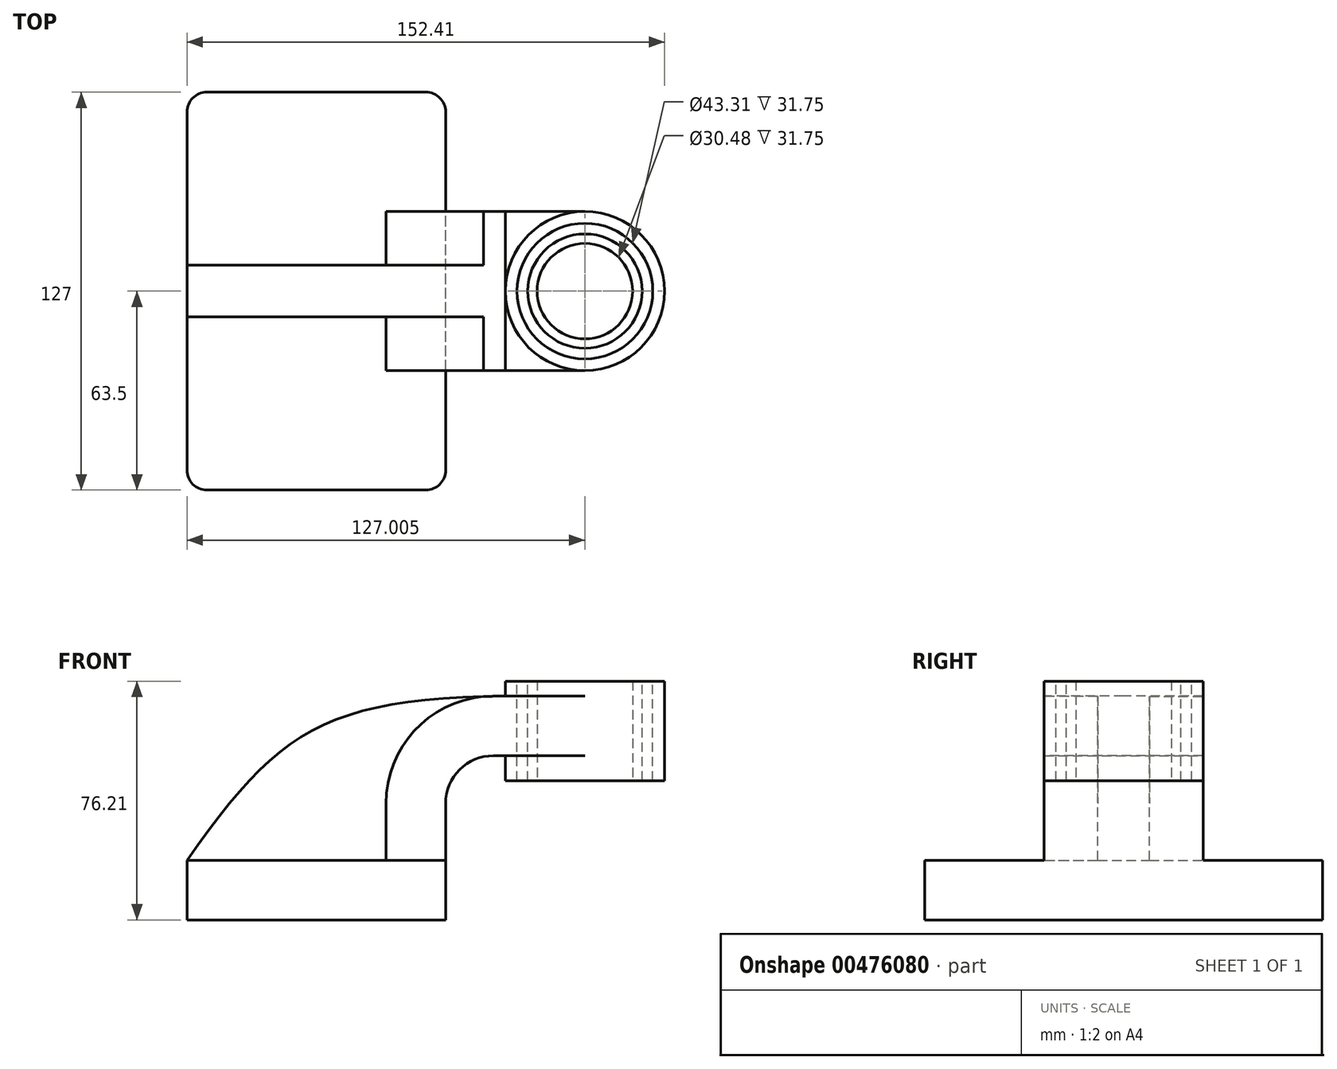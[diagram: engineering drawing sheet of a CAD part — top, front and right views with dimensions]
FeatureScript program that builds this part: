
annotation { "Feature Type Name" : "Feature", "Feature Type Description" : "" }
export const myFeature = defineFeature(function(context is Context, id is Id, definition is map)
    precondition{}
    {
        {
            var Q0;
            Q0=qCreatedBy(makeId("Front.planeOp"),FACE);
            var sketch = newSketch(context, id + "F0", { "sketchPlane" : qUnion([Q0])});
            skLineSegment(sketch, "E0.bottom", {"start": v(41.28, -9.52) * mm, "end": v(-41.27, -9.53) * mm});
            skLineSegment(sketch, "E0.top", {"start": v(41.27, 9.53) * mm, "end": v(-41.28, 9.53) * mm});
            skLineSegment(sketch, "E0.left", {"start": v(41.28, -9.52) * mm, "end": v(41.28, 9.53) * mm});
            skLineSegment(sketch, "E0.right", {"start": v(-41.27, -9.53) * mm, "end": v(-41.28, 9.53) * mm});
            skPoint(sketch, "E0.middle", {"position": v(0, 0) * mm});
            skLineSegment(sketch, "E1.bottom", {"start": v(111.12, 34.93) * mm, "end": v(60.32, 34.92) * mm});
            skLineSegment(sketch, "E1.top", {"start": v(111.12, 66.68) * mm, "end": v(85.72, 66.68) * mm});
            skLineSegment(sketch, "E1.left", {"start": v(111.13, 34.93) * mm, "end": v(111.13, 66.68) * mm});
            skLineSegment(sketch, "E1.right", {"start": v(60.32, 34.92) * mm, "end": v(60.32, 66.68) * mm});
            skPoint(sketch, "E1.middle", {"position": v(85.72, 50.8) * mm});
            skLineSegment(sketch, "E2", {"start": v(41.27, 9.53) * mm, "end": v(41.27, 27.64) * mm});
            skArc(sketch, "E3", {"start": v(41.27, 27.64) * mm, "mid": v(45.74, 38.41) * mm, "end": v(56.51, 42.88) * mm});
            skLineSegment(sketch, "E4", {"start": v(56.51, 42.88) * mm, "end": v(85.73, 42.88) * mm});
            skLineSegment(sketch, "E5.0", {"start": v(56.51, 61.93) * mm, "end": v(85.73, 61.93) * mm});
            skArc(sketch, "E5.1", {"start": v(22.22, 27.64) * mm, "mid": v(32.27, 51.88) * mm, "end": v(56.51, 61.93) * mm});
            skLineSegment(sketch, "E5.2", {"start": v(22.22, 9.53) * mm, "end": v(22.22, 27.64) * mm});
            skLineSegment(sketch, "E6", {"start": v(85.73, 61.93) * mm, "end": v(85.73, 42.88) * mm});
            skFitSpline(sketch, "E7", {"points": [v(-41.28, 9.52) * mm, v(60.32, 61.93) * mm], "startDerivative": vector(86.59, 123.54) * mm, "endDerivative": vector(173.56, 2.26) * mm});
            skLineSegment(sketch, "E8", {"start": v(85.72, 66.68) * mm, "end": v(85.72, 34.93) * mm});
            skSolve(sketch);
        }
        {
            var Q0;
            Q0=makeQuery(id+"F0.imprint","IMPRINT",FACE,{"disambiguationData":[TD([[makeQuery(id+"F0.imprint","IMPRINT",EDGE,{"derivedFrom":sQuery(id+"F0.wireOp",EDGE,"E0.bottom")}),-1.0]])]});
            extrude(context, id + "F1", {"entities" : qUnion([Q0]), "endBound" : BoundingType.SYMMETRIC, "depth" : 127 * mm});
        }
        {
            var Q0;
            {var subQ1=sQuery(id+"F0.wireOp",EDGE,"E2");Q0=makeQuery(id+"F0.imprint","IMPRINT",FACE,{"disambiguationData":[TD([[makeQuery(id+"F0.imprint","IMPRINT",EDGE,{"derivedFrom":subQ1}),1.0]])]});}
            var Q1;
            {var subQ3=sQuery(id+"F0.wireOp",EDGE,"E4");var subQ5=sQuery(id+"F0.wireOp",EDGE,"E8");var subQ6=makeQuery(id+"F0.imprint","INTERSECT",VERTEX,{"derivedFrom":[subQ3,subQ5]});Q1=makeQuery(id+"F0.imprint","IMPRINT",FACE,{"disambiguationData":[TD([[makeQuery(id+"F0.imprint","IMPRINT",EDGE,{"disambiguationData":[TD([[subQ6,1.0]])],"derivedFrom":subQ3}),1.0]])]});}
            extrude(context, id + "F2", {"entities" : qUnion([Q0, Q1]), "operationType" : NewBodyOperationType.ADD, "endBound" : BoundingType.SYMMETRIC, "depth" : 50.8 * mm});
        }
        {
            var Q0;
            {var subQ3=sQuery(id+"F0.wireOp",EDGE,"E5.2");Q0=makeQuery(id+"F0.imprint","IMPRINT",FACE,{"disambiguationData":[TD([[makeQuery(id+"F0.imprint","IMPRINT",EDGE,{"derivedFrom":subQ3}),1.0]])]});}
            extrude(context, id + "F3", {"entities" : qUnion([Q0]), "operationType" : NewBodyOperationType.ADD, "endBound" : BoundingType.SYMMETRIC, "depth" : 16.5 * mm});
        }
        {
            var Q0;
            {var subQ2=sQuery(id+"F0.wireOp",EDGE,"E1.top");Q0=makeQuery(id+"F0.imprint","IMPRINT",FACE,{"disambiguationData":[TD([[makeQuery(id+"F0.imprint","IMPRINT",EDGE,{"derivedFrom":subQ2}),1.0]])]});}
            var Q1;
            Q1=sQuery(id+"F0.wireOp",EDGE,"E8");
            revolve(context, id + "F4", {"operationType" : NewBodyOperationType.ADD, "entities" : qUnion([Q0]), "axis" : qUnion([Q1]), "revolveType" : RevolveType.FULL});
        }
        {
            var Q0;
            Q0=makeQuery(id+"F1.opExtrude","CAP_EDGE",EDGE,{"disambiguationData":[OSD([sQuery(id+"F0.wireOp",EDGE,"E0.right")])],"isStart":false});
            var Q1;
            Q1=makeQuery(id+"F1.opExtrude","CAP_EDGE",EDGE,{"disambiguationData":[OSD([sQuery(id+"F0.wireOp",EDGE,"E0.left")])],"isStart":false});
            var Q2;
            Q2=makeQuery(id+"F1.opExtrude","CAP_EDGE",EDGE,{"disambiguationData":[OSD([sQuery(id+"F0.wireOp",EDGE,"E0.left")])],"isStart":true});
            var Q3;
            Q3=makeQuery(id+"F1.opExtrude","CAP_EDGE",EDGE,{"disambiguationData":[OSD([sQuery(id+"F0.wireOp",EDGE,"E0.right")])],"isStart":true});
            fillet(context, id + "F5", {"entities" : qUnion([Q0, Q1, Q2, Q3]), "radius" : 6.35 * mm, "tangentPropagation" : true, "allowEdgeOverflow" : false});
        }
        {
            var Q0;
            Q0=qCreatedBy(makeId("Front.planeOp"),FACE);
            var sketch = newSketch(context, id + "F6", { "sketchPlane" : qUnion([Q0])});
            skLineSegment(sketch, "E9.bottom", {"start": v(85.72, 81.9) * mm, "end": v(100.96, 81.9) * mm});
            skLineSegment(sketch, "E9.top", {"start": v(85.72, 34.93) * mm, "end": v(100.96, 34.93) * mm});
            skLineSegment(sketch, "E9.left", {"start": v(85.72, 81.9) * mm, "end": v(85.72, 34.93) * mm});
            skLineSegment(sketch, "E9.right", {"start": v(100.96, 81.9) * mm, "end": v(100.96, 34.93) * mm});
            skSolve(sketch);
        }
        {
            var Q0;
            Q0=makeQuery(id+"F6.imprint","IMPRINT",FACE,{"disambiguationData":[TD([[makeQuery(id+"F6.imprint","IMPRINT",EDGE,{"derivedFrom":sQuery(id+"F6.wireOp",EDGE,"E9.bottom")}),-1.0]])]});
            var Q1;
            Q1=sQuery(id+"F6.wireOp",EDGE,"E9.left");
            revolve(context, id + "F7", {"operationType" : NewBodyOperationType.REMOVE, "entities" : qUnion([Q0]), "axis" : qUnion([Q1]), "revolveType" : RevolveType.FULL, "oppositeDirection" : true});
        }
        {
            var Q0;
            Q0=makeQuery(id+"F4.opRevolve","SWEPT_FACE",FACE,{"disambiguationData":[OSD([sQuery(id+"F0.wireOp",EDGE,"E1.top")])]});
            var sketch = newSketch(context, id + "F8", { "sketchPlane" : qUnion([Q0])});
            skLineSegment(sketch, "E10", {"start": v(60.32, 0) * mm, "end": v(111.12, 0) * mm});
            skCircle(sketch, "E11", {"center": v(85.72, 0) * mm, "radius": 18.24 * mm});
            skCircle(sketch, "E12.0", {"center": v(85.72, 0) * mm, "radius": 21.66 * mm});
            skSolve(sketch);
        }
        {
            var Q0;
            {var subQ0=sQuery(id+"F8.wireOp",EDGE,"E12.0");var subQ1=sQuery(id+"F8.wireOp",EDGE,"E10");var subQ2=makeQuery(id+"F8.imprint","INTERSECT",VERTEX,{"disambiguationData":[OD(0.0)],"derivedFrom":[subQ1,subQ0]});Q0=makeQuery(id+"F8.imprint","IMPRINT",FACE,{"disambiguationData":[TD([[makeQuery(id+"F8.imprint","IMPRINT",EDGE,{"disambiguationData":[TD([[subQ2,-1.0]])],"derivedFrom":subQ1}),1.0]])]});}
            var Q1;
            {var subQ0=sQuery(id+"F8.wireOp",EDGE,"E12.0");var subQ1=sQuery(id+"F8.wireOp",EDGE,"E10");var subQ2=makeQuery(id+"F8.imprint","INTERSECT",VERTEX,{"disambiguationData":[OD(0.0)],"derivedFrom":[subQ1,subQ0]});Q1=makeQuery(id+"F8.imprint","IMPRINT",FACE,{"disambiguationData":[TD([[makeQuery(id+"F8.imprint","IMPRINT",EDGE,{"disambiguationData":[TD([[subQ2,-1.0]])],"derivedFrom":subQ1}),-1.0]])]});}
            extrude(context, id + "F9", {"entities" : qUnion([Q0, Q1]), "operationType" : NewBodyOperationType.REMOVE, "oppositeDirection" : true, "depth" : 50.8 * mm});
        }
    });
